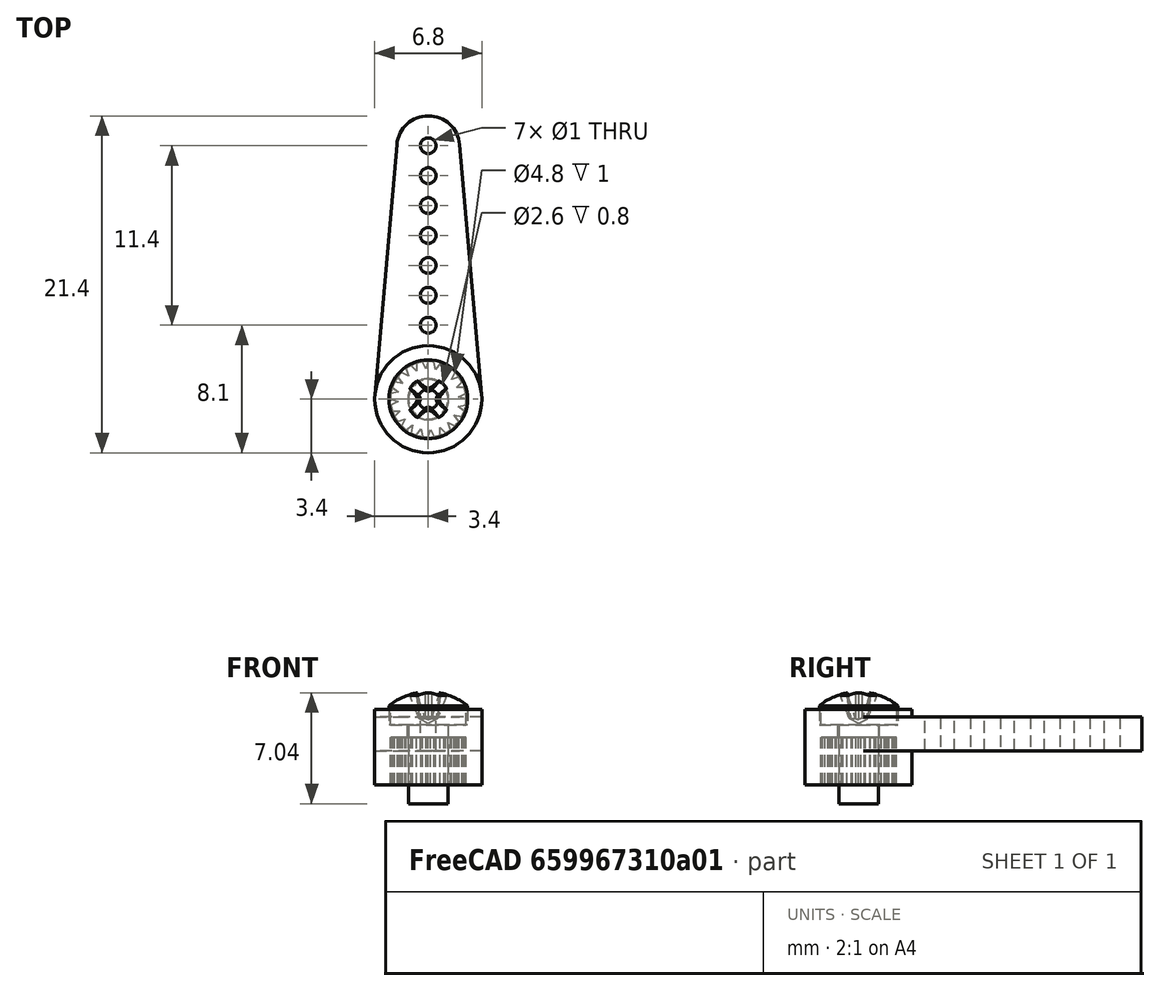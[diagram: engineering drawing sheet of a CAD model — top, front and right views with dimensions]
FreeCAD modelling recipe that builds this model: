
FCSTD DOCUMENT  (FreeCAD 0.21R33771 (Git))
Label: mg90s_with_arm
License: All rights reserved
LicenseURL: http://en.wikipedia.org/wiki/All_rights_reserved
objects: App::FeaturePython×4, Part::FeaturePython×3
note: 3 computed .brp shape members not serialized (recipe doc carries the construction recipe); baked Part::Feature solids carry a one-line shape summary decoded from their .brp

FEATURE [Part::FeaturePython] b_M90S_ali_001_  label="M90S_ali_001"  # a2plus imported part (geometry in sourceFile) (typed FeaturePython)
  a2p_Version = 0.4.65
  fixedPosition = true
  objectType = a2pPart
  sourceFile = .\M90S_ali.FCStd
  subassemblyImport = false
  timeLastImport = 1.7252e+09
  updateColors = true
FEATURE [Part::FeaturePython] b_MG90S_bras_01_001_  label="MG90S_bras_01_001"  # a2plus imported part (geometry in sourceFile) (typed FeaturePython)
  Placement = pos=(-2.8076e-12,5.694e-13,16) rot=(0,1,0;1.5708rad)
  a2p_Version = 0.4.65
  fixedPosition = false
  objectType = a2pPart
  sourceFile = .\MG90S_bras_01.FCStd
  subassemblyImport = false
  timeLastImport = 1.72522e+09
  updateColors = true
FEATURE [App::FeaturePython] axisCoincident_001  label="axisCoincident_001__M90S_ali_001"  # a2plus constraint (typed FeaturePython)
  Object1 = b_MG90S_bras_01_001_
  Object2 = b_M90S_ali_001_
  ParentTreeObject = -> b_MG90S_bras_01_001_
  SubElement1 = Edge44
  SubElement2 = Edge67
  Suppressed = false
  Type = axial
  directionConstraint = 1
  lockRotation = false
FEATURE [App::FeaturePython] axisCoincident_001_mirror  label="axisCoincident_001__MG90S_bras_01_001"  # a2plus constraint (typed FeaturePython)
  Object1 = b_MG90S_bras_01_001_
  Object2 = b_M90S_ali_001_
  ParentTreeObject = -> b_M90S_ali_001_
  SubElement1 = Edge44
  SubElement2 = Edge67
  Suppressed = false
  Type = axial
  directionConstraint = 1
  lockRotation = false
FEATURE [App::FeaturePython] planeCoincident_001  label="planeCoincident_001__M90S_ali_001"  # a2plus constraint (typed FeaturePython)
  Object1 = b_MG90S_bras_01_001_
  Object2 = b_M90S_ali_001_
  ParentTreeObject = -> b_MG90S_bras_01_001_
  SubElement1 = Face96
  SubElement2 = Face113
  Suppressed = false
  Type = plane
  directionConstraint = 1
  offset = 0
FEATURE [App::FeaturePython] planeCoincident_001_mirror  label="planeCoincident_001__MG90S_bras_01_001"  # a2plus constraint (typed FeaturePython)
  Object1 = b_MG90S_bras_01_001_
  Object2 = b_M90S_ali_001_
  ParentTreeObject = -> b_M90S_ali_001_
  SubElement1 = Face96
  SubElement2 = Face113
  Suppressed = false
  Type = plane
  directionConstraint = 1
  offset = 0
FEATURE [Part::FeaturePython] Screw  label="M2.5x5-Screw"  # Fasteners workbench fastener (typed FeaturePython)
  Placement = pos=(-2.8081e-12,5.687e-13,15) rot=(0,0,1;0rad)
  baseObject = -> b_MG90S_bras_01_001_ [Edge45]
  diameter = 3
  invert = false
  leftHanded = false
  length = 2
  lengthCustom = 5
  matchOuter = false
  offset = 0
  thread = false
  type = 46
